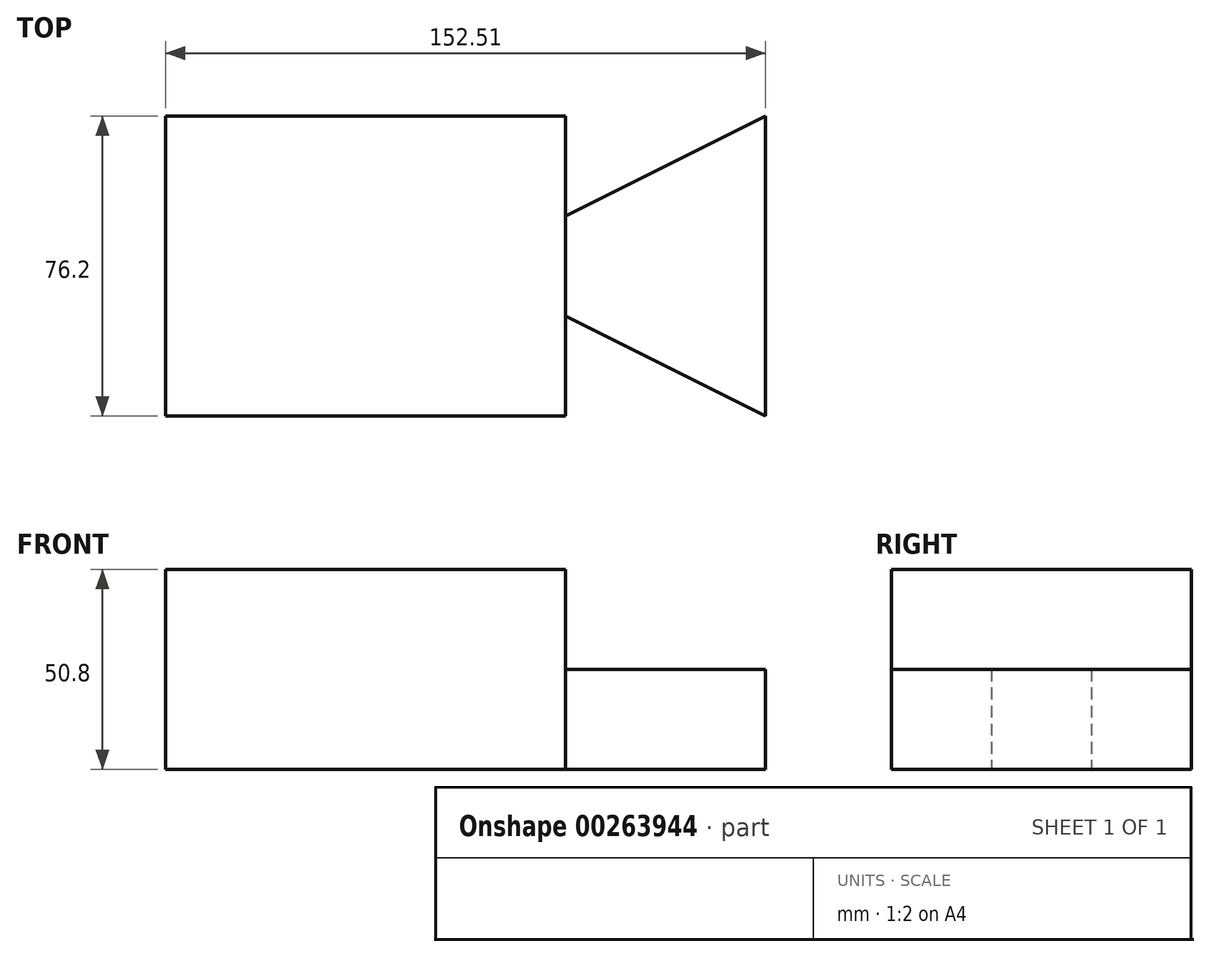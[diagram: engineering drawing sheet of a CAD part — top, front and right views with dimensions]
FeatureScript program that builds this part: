
annotation { "Feature Type Name" : "Feature", "Feature Type Description" : "" }
export const myFeature = defineFeature(function(context is Context, id is Id, definition is map)
    precondition{}
    {
        {
            var Q0;
            Q0=qCreatedBy(makeId("Front.planeOp"),FACE);
            var sketch = newSketch(context, id + "F0", { "sketchPlane" : qUnion([Q0])});
            skLineSegment(sketch, "E0", {"start": v(0, 0) * mm, "end": v(-101.6, 0) * mm});
            skLineSegment(sketch, "E1", {"start": v(-101.6, 0) * mm, "end": v(-101.6, 50.8) * mm});
            skLineSegment(sketch, "E2", {"start": v(-101.6, 50.8) * mm, "end": v(0, 50.8) * mm});
            skLineSegment(sketch, "E3", {"start": v(0, 50.8) * mm, "end": v(0, 0) * mm});
            skSolve(sketch);
        }
        {
            var Q0;
            Q0 = qSketchRegion(id + "F0", true);
            extrude(context, id + "F1", {"entities" : qUnion([Q0]), "depth" : 76.2 * mm});
        }
        {
            var Q0;
            Q0=makeQuery(id+"F1.opExtrude","SWEPT_FACE",FACE,{"disambiguationData":[OSD([sQuery(id+"F0.wireOp",EDGE,"E0")])]});
            var sketch = newSketch(context, id + "F2", { "sketchPlane" : qUnion([Q0])});
            skLineSegment(sketch, "E4", {"start": v(0, 0) * mm, "end": v(0, 25.4) * mm});
            skLineSegment(sketch, "E5", {"start": v(0, 25.4) * mm, "end": v(50.8, 25.4) * mm, "construction": true});
            skLineSegment(sketch, "E6", {"start": v(0, 76.2) * mm, "end": v(0, 50.8) * mm});
            skLineSegment(sketch, "E7", {"start": v(0, 50.8) * mm, "end": v(50.8, 50.8) * mm, "construction": true});
            skLineSegment(sketch, "E8", {"start": v(50.8, 50.8) * mm, "end": v(50.8, 25.4) * mm, "construction": true});
            skLineSegment(sketch, "E9", {"start": v(0, 25.4) * mm, "end": v(50.9, 0) * mm});
            skLineSegment(sketch, "E10", {"start": v(50.9, 0) * mm, "end": v(50.8, 76.2) * mm});
            skLineSegment(sketch, "E11", {"start": v(50.8, 76.2) * mm, "end": v(0, 50.8) * mm});
            skSolve(sketch);
        }
        {
            var Q0;
            {var subQ0=sQuery(id+"F2.wireOp",EDGE,"E9");Q0=makeQuery(id+"F2.imprint","IMPRINT",FACE,{"disambiguationData":[TD([[makeQuery(id+"F2.imprint","IMPRINT",EDGE,{"derivedFrom":subQ0}),1.0]])]});}
            extrude(context, id + "F3", {"entities" : qUnion([Q0]), "oppositeDirection" : true, "depth" : 25.4 * mm});
        }
    });
